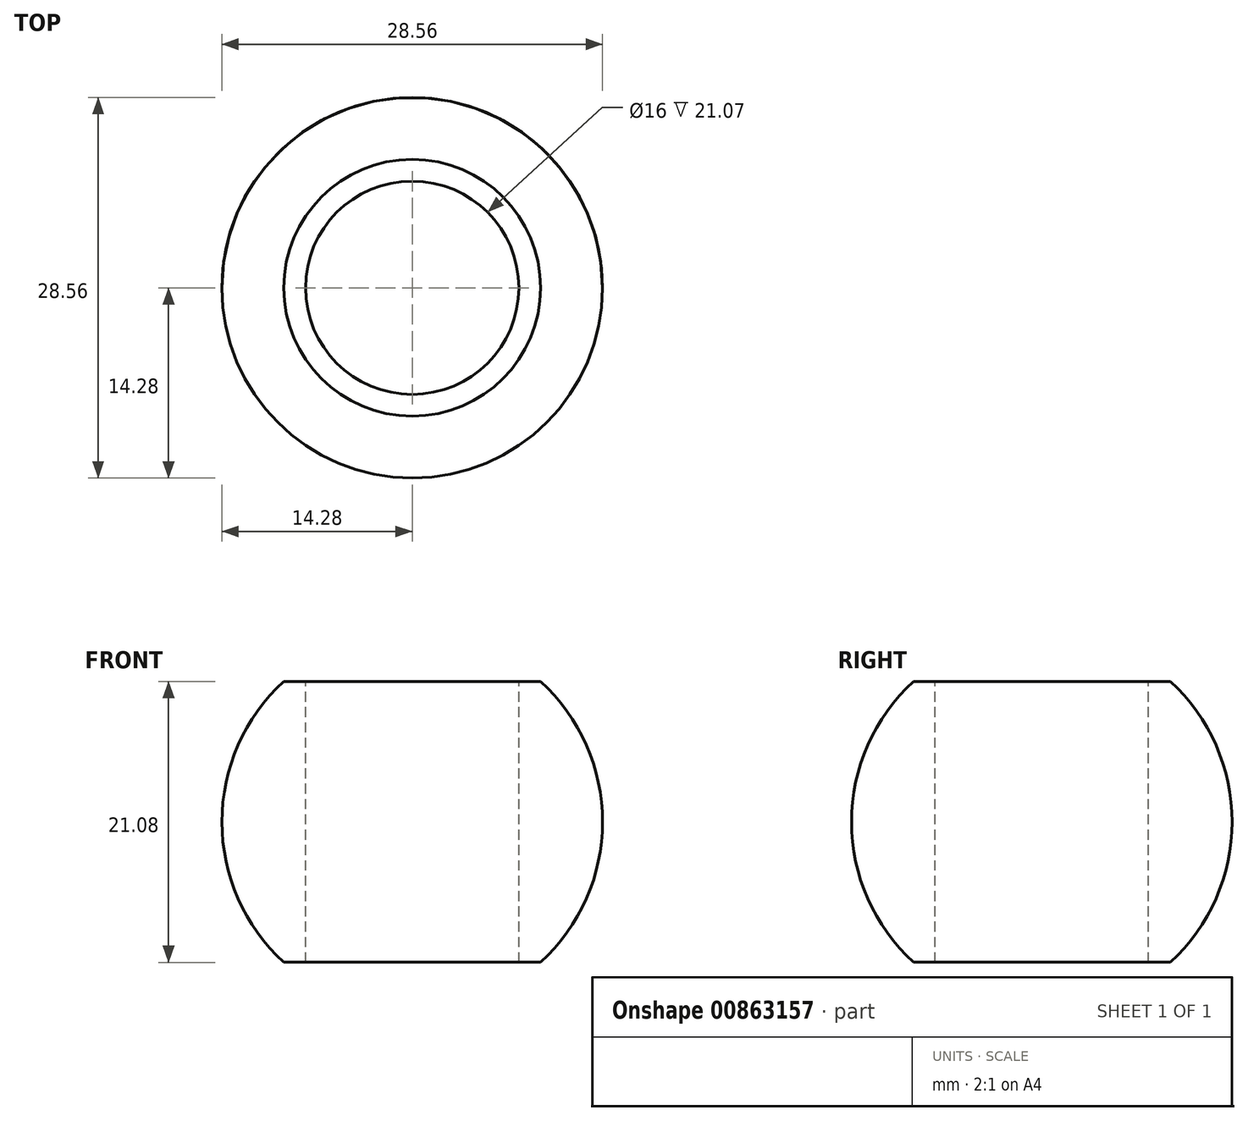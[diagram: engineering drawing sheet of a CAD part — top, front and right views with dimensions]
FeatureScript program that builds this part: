
annotation { "Feature Type Name" : "Feature", "Feature Type Description" : "" }
export const myFeature = defineFeature(function(context is Context, id is Id, definition is map)
    precondition{}
    {
        {
            var Q0;
            Q0=qCreatedBy(makeId("Top.planeOp"),FACE);
            var sketch = newSketch(context, id + "F0", { "sketchPlane" : qUnion([Q0])});
            skArc(sketch, "E0", {"start": v(14.28, 0) * mm, "mid": v(0, 14.28) * mm, "end": v(-14.28, 0) * mm});
            skLineSegment(sketch, "E1", {"start": v(-14.28, 0) * mm, "end": v(14.28, 0) * mm});
            skSolve(sketch);
        }
        {
            var Q0;
            Q0 = qSketchRegion(id + "F0", true);
            var Q1;
            Q1=sQuery(id+"F0.wireOp",EDGE,"E1");
            revolve(context, id + "F1", {"surfaceOperationType" : NewSurfaceOperationType.NEW, "entities" : qUnion([Q0]), "axis" : qUnion([Q1]), "revolveType" : RevolveType.FULL});
        }
        {
            var Q0;
            Q0=qCreatedBy(makeId("Front.planeOp"),FACE);
            var sketch = newSketch(context, id + "F2", { "sketchPlane" : qUnion([Q0])});
            skLineSegment(sketch, "E2.bottom", {"start": v(-20, 20.53) * mm, "end": v(20, 20.54) * mm});
            skLineSegment(sketch, "E2.top", {"start": v(-20, 10.54) * mm, "end": v(20, 10.54) * mm});
            skLineSegment(sketch, "E2.left", {"start": v(-20, 20.53) * mm, "end": v(-20, 10.53) * mm});
            skLineSegment(sketch, "E2.right", {"start": v(20, 20.54) * mm, "end": v(20, 10.54) * mm});
            skLineSegment(sketch, "E3.MirrorCS", {"start": v(-20, -10.54) * mm, "end": v(20, -10.54) * mm});
            skLineSegment(sketch, "E4.MirrorCS", {"start": v(-20, -20.53) * mm, "end": v(-20, -10.53) * mm});
            skLineSegment(sketch, "E5.MirrorCS", {"start": v(-20, -20.53) * mm, "end": v(20, -20.54) * mm});
            skLineSegment(sketch, "E6.MirrorCS", {"start": v(20, -20.54) * mm, "end": v(20, -10.54) * mm});
            skSolve(sketch);
        }
        {
            var Q0;
            Q0 = qSketchRegion(id + "F2", true);
            extrude(context, id + "F3", {"entities" : qUnion([Q0]), "operationType" : NewBodyOperationType.REMOVE, "endBound" : BoundingType.SYMMETRIC, "oppositeDirection" : true, "depth" : 25 * mm, "offsetDistance" : 25 * mm});
        }
        {
            var Q0;
            Q0=makeQuery(id+"F3.boolean.opBoolean","COPY",FACE,{"derivedFrom":makeQuery(id+"F3.opExtrude","SWEPT_FACE",FACE,{"disambiguationData":[OSD([sQuery(id+"F2.wireOp",EDGE,"E2.top")])]})});
            var sketch = newSketch(context, id + "F4", { "sketchPlane" : qUnion([Q0])});
            skCircle(sketch, "E7", {"center": v(0, 0) * mm, "radius": 8 * mm});
            skSolve(sketch);
        }
        {
            var Q0;
            Q0 = qSketchRegion(id + "F4", true);
            extrude(context, id + "F5", {"entities" : qUnion([Q0]), "operationType" : NewBodyOperationType.REMOVE, "endBound" : BoundingType.THROUGH_ALL, "oppositeDirection" : true, "depth" : 25 * mm, "offsetDistance" : 25 * mm});
        }
    });
